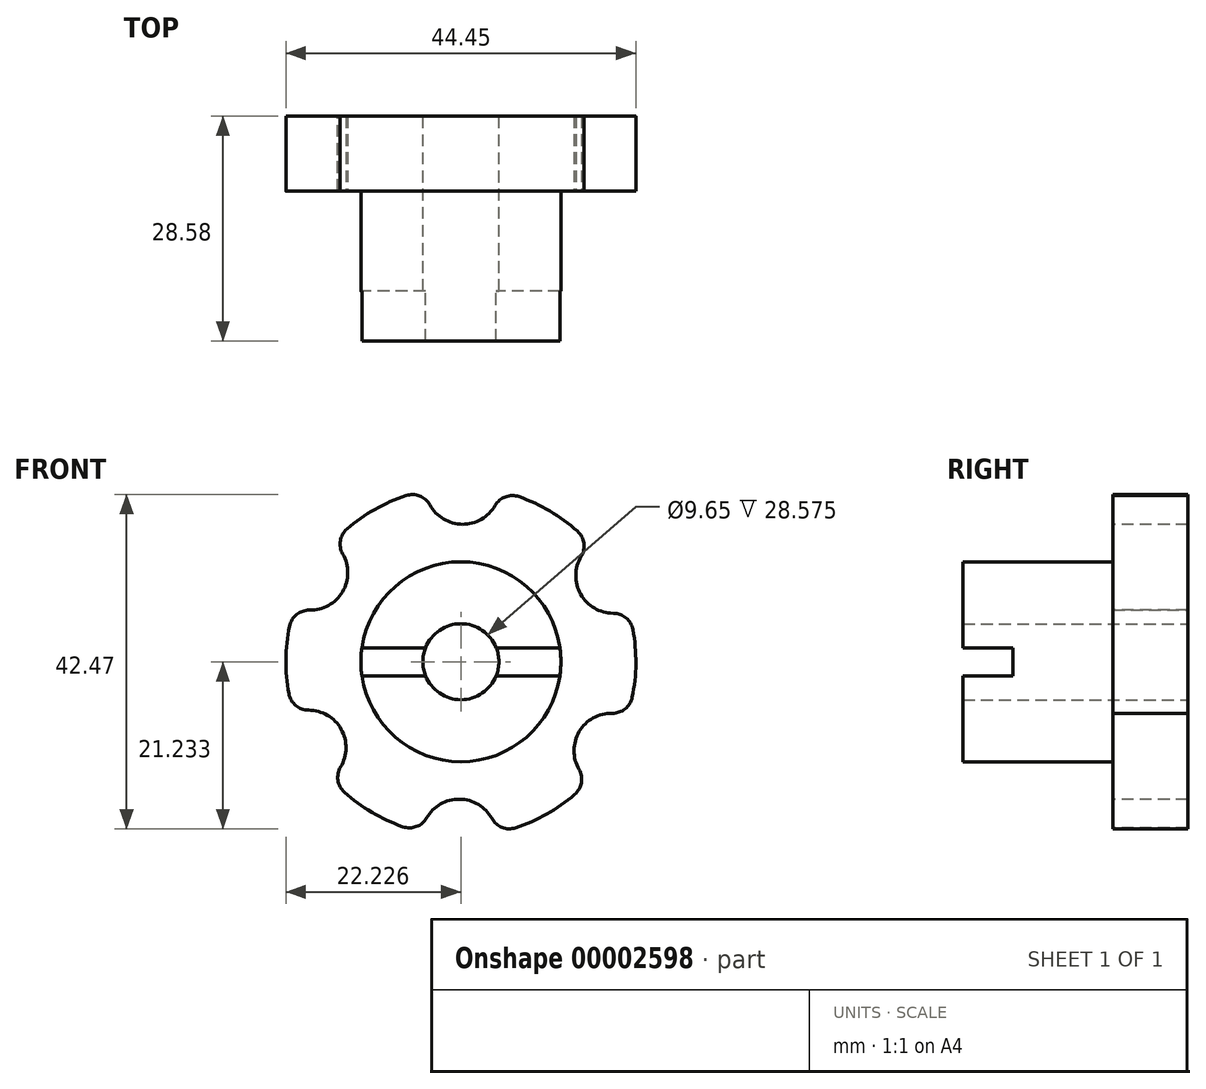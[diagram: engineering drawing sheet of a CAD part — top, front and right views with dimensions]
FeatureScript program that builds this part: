
annotation { "Feature Type Name" : "Feature", "Feature Type Description" : "" }
export const myFeature = defineFeature(function(context is Context, id is Id, definition is map)
    precondition{}
    {
        {
            var Q0;
            Q0=qCreatedBy(makeId("Front.planeOp"),FACE);
            var sketch = newSketch(context, id + "F0", { "sketchPlane" : qUnion([Q0])});
            skCircle(sketch, "E0", {"center": v(-26.43, 19.35) * mm, "radius": 22.23 * mm});
            skCircle(sketch, "E1", {"center": v(-26.43, 19.35) * mm, "radius": 12.7 * mm});
            skCircle(sketch, "E2", {"center": v(-26.43, 19.35) * mm, "radius": 4.83 * mm});
            skSolve(sketch);
        }
        {
            var Q0;
            Q0=makeQuery(id+"F0.imprint","IMPRINT",FACE,{"disambiguationData":[TD([[makeQuery(id+"F0.imprint","IMPRINT",EDGE,{"derivedFrom":sQuery(id+"F0.wireOp",EDGE,"E1")}),1.0]])]});
            extrude(context, id + "F1", {"entities" : qUnion([Q0]), "depth" : 19.05 * mm});
        }
        {
            var Q0;
            Q0 = qSketchRegion(id + "F0", true);
            extrude(context, id + "F2", {"entities" : qUnion([Q0]), "operationType" : NewBodyOperationType.ADD, "oppositeDirection" : true, "depth" : 9.52 * mm});
        }
        {
            var Q0;
            Q0=makeQuery(id+"F1.opExtrude","CAP_FACE",FACE,{"disambiguationData":[OSD([sQuery(id+"F0.wireOp",EDGE,"E1"),sQuery(id+"F0.wireOp",EDGE,"E2")])],"isStart":true});
            extrude(context, id + "F3", {"entities" : qUnion([Q0]), "operationType" : NewBodyOperationType.ADD, "depth" : 9.52 * mm});
        }
        {
            var Q0;
            Q0=makeQuery(id+"F1.opExtrude","CAP_FACE",FACE,{"disambiguationData":[OSD([sQuery(id+"F0.wireOp",EDGE,"E1"),sQuery(id+"F0.wireOp",EDGE,"E2")])],"isStart":false});
            var sketch = newSketch(context, id + "F4", { "sketchPlane" : qUnion([Q0])});
            skLineSegment(sketch, "E3.rect.bottom", {"start": v(-13.73, 17.58) * mm, "end": v(-39.13, 17.58) * mm});
            skLineSegment(sketch, "E3.rect.top", {"start": v(-13.73, 21.13) * mm, "end": v(-39.13, 21.13) * mm});
            skLineSegment(sketch, "E3.rect.left", {"start": v(-13.73, 17.58) * mm, "end": v(-13.73, 21.13) * mm});
            skLineSegment(sketch, "E3.rect.right", {"start": v(-39.13, 17.58) * mm, "end": v(-39.13, 21.13) * mm});
            skPoint(sketch, "E3.rect.middle", {"position": v(-26.43, 19.35) * mm});
            skSolve(sketch);
        }
        {
            var Q0;
            Q0 = qSketchRegion(id + "F4", true);
            extrude(context, id + "F5", {"entities" : qUnion([Q0]), "operationType" : NewBodyOperationType.REMOVE, "oppositeDirection" : true, "depth" : 6.35 * mm});
        }
        {
            var Q0;
            {var subQ0=sQuery(id+"F0.wireOp",EDGE,"E1");Q0=makeQuery(id+"F3.boolean.opBoolean","MERGE",FACE,{"derivedFrom":[makeQuery(id+"F2.opExtrude","CAP_FACE",FACE,{"disambiguationData":[OSD([sQuery(id+"F0.wireOp",EDGE,"E0"),subQ0])],"isStart":true}),makeQuery(id+"F3.opExtrude","CAP_FACE",FACE,{"disambiguationData":[OSD([subQ0,sQuery(id+"F0.wireOp",EDGE,"E2")])],"isStart":true})]});}
            var sketch = newSketch(context, id + "F6", { "sketchPlane" : qUnion([Q0])});
            skCircle(sketch, "E4", {"center": v(-26.2, 41.58) * mm, "radius": 4.76 * mm});
            skSolve(sketch);
        }
        {
            var Q0;
            {var subQ0=makeQuery(id+"F2.opExtrude","CAP_EDGE",EDGE,{"disambiguationData":[OSD([sQuery(id+"F0.wireOp",EDGE,"E0")])],"isStart":true});var subQ1=sQuery(id+"F6.wireOp",EDGE,"E4");var subQ3=makeQuery(id+"F6.imprint","INTERSECT",VERTEX,{"disambiguationData":[OD(0.0)],"derivedFrom":[subQ0,subQ1]});Q0=makeQuery(id+"F6.imprint","IMPRINT",FACE,{"disambiguationData":[TD([[makeQuery(id+"F6.imprint","IMPRINT",EDGE,{"disambiguationData":[TD([[subQ3,1.0]])],"derivedFrom":subQ1}),1.0]])]});}
            var Q1;
            {var subQ0=makeQuery(id+"F2.opExtrude","CAP_EDGE",EDGE,{"disambiguationData":[OSD([sQuery(id+"F0.wireOp",EDGE,"E0")])],"isStart":true});var subQ1=sQuery(id+"F6.wireOp",EDGE,"E4");var subQ3=makeQuery(id+"F6.imprint","INTERSECT",VERTEX,{"disambiguationData":[OD(0.0)],"derivedFrom":[subQ0,subQ1]});Q1=makeQuery(id+"F6.imprint","IMPRINT",FACE,{"disambiguationData":[TD([[makeQuery(id+"F6.imprint","IMPRINT",EDGE,{"disambiguationData":[TD([[subQ3,-1.0]])],"derivedFrom":subQ1}),1.0]])]});}
            var Q2;
            Q2=sQuery(id+"F6.wireOp",EDGE,"E4");
            extrude(context, id + "F7", {"entities" : qUnion([Q0, Q1]), "operationType" : NewBodyOperationType.REMOVE, "surfaceEntities" : qUnion([Q2]), "oppositeDirection" : true, "depth" : 25.4 * mm});
        }
        {
            var Q0;
            Q0=makeQuery(id+"F7.boolean.opBoolean","INTERSECT",EDGE,{"disambiguationData":[OD(1.0)],"derivedFrom":[makeQuery(id+"F2.opExtrude","SWEPT_FACE",FACE,{"disambiguationData":[OSD([sQuery(id+"F0.wireOp",EDGE,"E0")])]}),makeQuery(id+"F7.opExtrude","SWEPT_FACE",FACE,{"disambiguationData":[OSD([sQuery(id+"F6.wireOp",EDGE,"E4")])]})]});
            var Q1;
            Q1=makeQuery(id+"F7.boolean.opBoolean","INTERSECT",EDGE,{"disambiguationData":[OD(0.0)],"derivedFrom":[makeQuery(id+"F2.opExtrude","SWEPT_FACE",FACE,{"disambiguationData":[OSD([sQuery(id+"F0.wireOp",EDGE,"E0")])]}),makeQuery(id+"F7.opExtrude","SWEPT_FACE",FACE,{"disambiguationData":[OSD([sQuery(id+"F6.wireOp",EDGE,"E4")])]})]});
            fillet(context, id + "F8", {"entities" : qUnion([Q0, Q1]), "radius" : 2.54 * mm, "tangentPropagation" : true, "allowEdgeOverflow" : false});
        }
        {
            var Q0;
            {var subQ0=sQuery(id+"F0.wireOp",EDGE,"E0");var subQ1=sQuery(id+"F6.wireOp",EDGE,"E4");Q0=makeQuery(id+"F8.opFillet","BLEND_FACE",FACE,{"disambiguationData":[OSD([subQ0,subQ1]),TDD([makeQuery(id+"F7.boolean.opBoolean","INTERSECT",EDGE,{"disambiguationData":[OD(1.0)],"derivedFrom":[makeQuery(id+"F2.opExtrude","SWEPT_FACE",FACE,{"disambiguationData":[OSD([subQ0])]}),makeQuery(id+"F7.opExtrude","SWEPT_FACE",FACE,{"disambiguationData":[OSD([subQ1])]})]})])]});}
            var Q1;
            Q1=makeQuery(id+"F7.boolean.opBoolean","COPY",FACE,{"derivedFrom":makeQuery(id+"F7.opExtrude","SWEPT_FACE",FACE,{"disambiguationData":[OSD([sQuery(id+"F6.wireOp",EDGE,"E4")])]})});
            var Q2;
            {var subQ0=sQuery(id+"F0.wireOp",EDGE,"E0");var subQ1=sQuery(id+"F6.wireOp",EDGE,"E4");Q2=makeQuery(id+"F8.opFillet","BLEND_FACE",FACE,{"disambiguationData":[OSD([subQ0,subQ1]),TDD([makeQuery(id+"F7.boolean.opBoolean","INTERSECT",EDGE,{"disambiguationData":[OD(0.0)],"derivedFrom":[makeQuery(id+"F2.opExtrude","SWEPT_FACE",FACE,{"disambiguationData":[OSD([subQ0])]}),makeQuery(id+"F7.opExtrude","SWEPT_FACE",FACE,{"disambiguationData":[OSD([subQ1])]})]})])]});}
            var Q3;
            Q3=makeQuery(id+"F1.opExtrude","SWEPT_FACE",FACE,{"disambiguationData":[OSD([sQuery(id+"F0.wireOp",EDGE,"E1")])]});
            circularPattern(context, id + "F9", {"faces" : qUnion([Q0, Q1, Q2]), "axis" : qUnion([Q3]), "angle" : 60 * degree, "instanceCount" : 6, "patternType" : PatternType.FACE});
        }
    });
